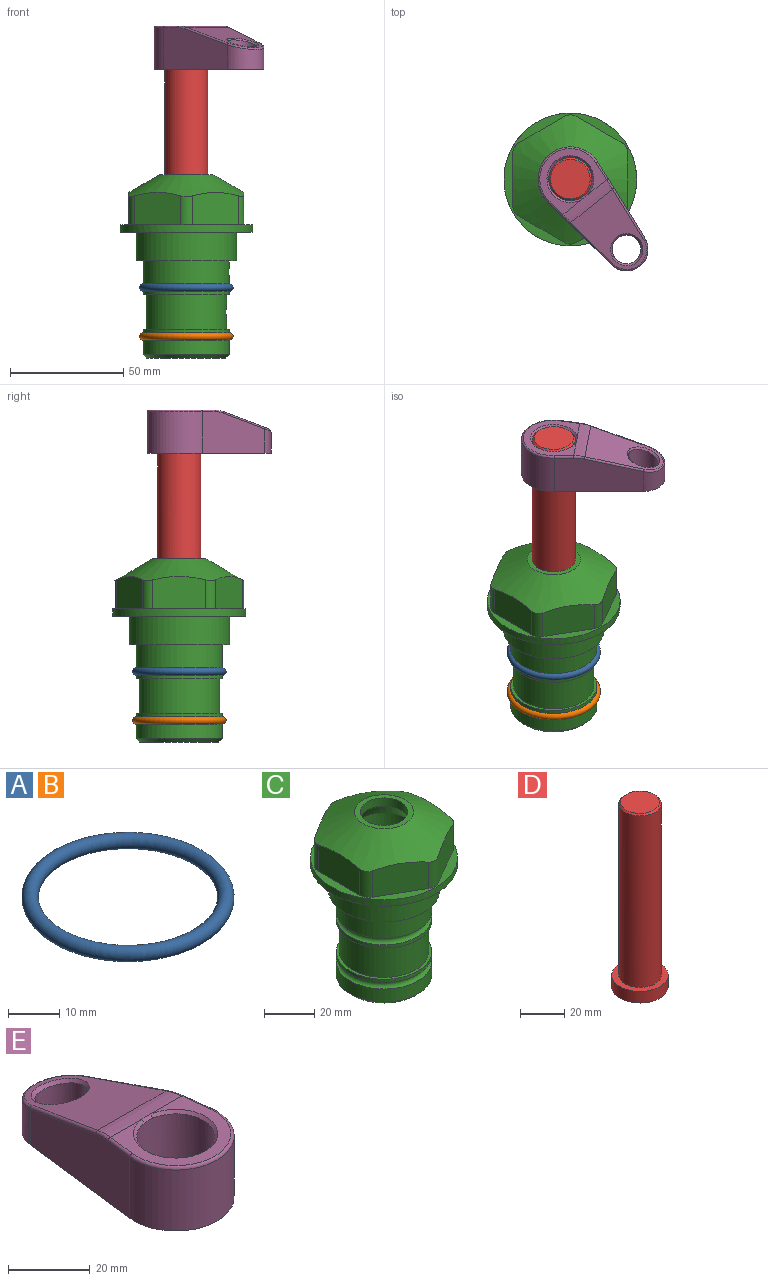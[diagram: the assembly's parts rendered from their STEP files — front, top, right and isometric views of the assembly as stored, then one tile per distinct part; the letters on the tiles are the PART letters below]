
ASSEMBLY  parts=5 mates=4
PART A: 1 faces, bbox 44.7x44.7x3.2 mm
  f0: torus R=19.05mm, axis (0,0,1), area 1193.9mm2
PART B: same geometry as A
PART C: 36 faces, bbox 58.7x58.7x81 mm
  f0: cylinder r=17.78mm len=35.56mm, axis (0,0,1), area 1670.8mm2, adj f23,f24,f31
  f1: cylinder r=19.05mm len=38.1mm, axis (0,0,1), area 1191.9mm2, adj f26,f27,f30
  f2: plane 58.66x58.66mm, normal (0,0,-1), area 1150.6mm2, adj f3,f28
  f3: cylinder r=29.33mm len=58.66mm, axis (0,0,-1), area 585.1mm2, adj f2,f4
  f4: plane 58.66x58.66mm, normal (0,0,1), area 475.9mm2, adj f3,f5,f6,f7,f8,f9,f10,f11
  f5: plane 20.32x14.34mm, normal (-0.5,0.87,0), area 324.4mm2, adj f4,f15,f16,f17
  f6: plane 20.32x14.34mm, normal (0.5,0.87,0), area 324.4mm2, adj f4,f14,f15,f17
  f7: plane 23.48x14.34mm, normal (1,0,0), area 324.4mm2, adj f4,f13,f14,f17
  f8: plane 20.32x14.34mm, normal (0.5,-0.87,0), area 324.4mm2, adj f4,f12,f13,f17
  f9: plane 20.32x14.34mm, normal (-0.5,-0.87,0), area 324.4mm2, adj f4,f11,f12,f17
  f10: plane 23.48x14.34mm, normal (-1,0,0), area 324.4mm2, adj f4,f11,f16,f17
  f11: cylinder r=5.08mm len=12.85mm, axis (0,0,-1), area 67.2mm2, adj f4,f9,f10,f17
  f12: cylinder r=5.08mm len=12.85mm, axis (0,0,-1), area 67.2mm2, adj f4,f8,f9,f17
  f13: cylinder r=5.08mm len=12.85mm, axis (0,0,-1), area 67.2mm2, adj f4,f7,f8,f17
  f14: cylinder r=5.08mm len=12.85mm, axis (0,0,-1), area 67.2mm2, adj f4,f6,f7,f17
  f15: cylinder r=5.08mm len=12.85mm, axis (0,0,-1), area 67.2mm2, adj f4,f5,f6,f17
  f16: cylinder r=5.08mm len=12.85mm, axis (0,0,-1), area 67.2mm2, adj f4,f5,f10,f17
  f17: cone r=11.73mm half-angle=60deg, axis (0,0,-1), area 2071.8mm2, adj f5,f6,f7,f8,f9,f10,f11,f12
  f18: plane 23.46x23.46mm, normal (0,0,1), area 147.4mm2, adj f17,f35
  f19: plane 34.93x34.93mm, normal (0,0,-1), area 958mm2, adj f29
  f20: cylinder r=19.05mm len=38.1mm, axis (0,0,1), area 760.1mm2, adj f21,f29
  f21: torus R=19.05mm, axis (0,0,1), area 565.3mm2, adj f20,f22
  f22: cylinder r=19.05mm len=38.1mm, axis (0,0,1), area 190mm2, adj f21,f23
  f23: plane 38.1x38.1mm, normal (0,0,1), area 146.9mm2, adj f0,f22
  f24: plane 38.1x38.1mm, normal (0,0,-1), area 146.9mm2, adj f0,f25
  f25: cylinder r=19.05mm len=38.1mm, axis (0,0,1), area 190mm2, adj f24,f26
  f26: torus R=19.05mm, axis (0,0,1), area 565.3mm2, adj f1,f25
  f27: plane 44.45x44.45mm, normal (0,0,-1), area 411.7mm2, adj f1,f28
  f28: cylinder r=22.23mm len=44.45mm, axis (0,0,1), area 1773.5mm2, adj f2,f27
  f29: cone r=19.05mm half-angle=45deg, axis (0,0,1), area 257.5mm2, adj f19,f20
  f30: cylinder r=3.17mm len=6.75mm, axis (-1,0,0), area 128mm2, adj f1,f33
  f31: cylinder r=3.17mm len=6.35mm, axis (-1,0,0), area 102.5mm2, adj f0,f33
  f32: plane 25.4x25.4mm, normal (0,0,1), area 506.7mm2, adj f33
  f33: cylinder r=12.7mm len=66.42mm, axis (0,0,-1), area 5236.2mm2, adj f30,f31,f32,f34
  f34: cone r=9.53mm half-angle=30deg, axis (0,0,-1), area 443.4mm2, adj f33,f35
  f35: cylinder r=9.53mm len=19.05mm, axis (0,0,-1), area 240.9mm2, adj f18,f34
PART D: 6 faces, bbox 25.4x25.4x101.6 mm
  f0: plane 17.46x17.46mm, normal (0,0,1), area 239.5mm2, adj f5
  f1: plane 25.4x25.4mm, normal (0,0,-1), area 506.7mm2, adj f2
  f2: cylinder r=12.7mm len=25.4mm, axis (0,0,1), area 506.7mm2, adj f1,f3
  f3: plane 25.4x25.4mm, normal (0,0,1), area 221.7mm2, adj f2,f4
  f4: cylinder r=9.53mm len=94.46mm, axis (0,0,1), area 5653mm2, adj f3,f5
  f5: cone r=8.73mm half-angle=45deg, axis (0,0,-1), area 64.4mm2, adj f0,f4
PART E: 31 faces, bbox 31.7x65.5x19.8 mm
  f0: plane 39.12x18.26mm, normal (0.99,0.12,0), area 612.2mm2, adj f1,f4,f7,f11,f13,f15
  f1: cylinder r=9.53mm len=18.91mm, axis (0,0,-1), area 296.1mm2, adj f0,f2,f7,f17
  f2: plane 39.12x18.26mm, normal (-0.99,0.12,0), area 612.2mm2, adj f1,f4,f7,f12,f14,f16
  f3: cylinder r=6.35mm len=12.7mm, axis (0,0,-1), area 362.4mm2, adj f7,f18
  f4: cylinder r=14.29mm len=28.58mm, axis (0,0,-1), area 882.2mm2, adj f0,f2,f7,f10
  f5: cylinder r=9.53mm len=19.05mm, axis (0,0,-1), area 1092.6mm2, adj f7,f19,f20
  f6: plane 26.99x23.69mm, normal (0,0,1), area 216.2mm2, adj f9,f10,f11,f12,f19
  f7: plane 63.5x28.58mm, normal (0,0,-1), area 661.8mm2, adj f0,f1,f2,f3,f4,f5,f22,f23
  f8: plane 33.52x23.6mm, normal (0,0.26,0.97), area 486mm2, adj f9,f15,f16,f17,f18
  f9: cylinder r=19.05mm len=24.72mm, axis (1,0,0), area 120.4mm2, adj f6,f8,f13,f14,f20
  f10: torus R=13.49mm, axis (0,0,1), area 59mm2, adj f4,f6,f11,f12
  f11: cylinder r=0.79mm len=8.67mm, axis (0.12,-0.99,0), area 10.8mm2, adj f0,f6,f10,f13
  f12: cylinder r=0.79mm len=8.67mm, axis (0.12,0.99,0), area 10.8mm2, adj f2,f6,f10,f14
  f13: bspline ~4.95x1.42mm, area 6.1mm2, adj f0,f9,f11,f15
  f14: bspline ~4.95x1.42mm, area 6.1mm2, adj f2,f9,f12,f16
  f15: cylinder r=0.79mm len=25.95mm, axis (0.12,-0.96,0.26), area 32.9mm2, adj f0,f8,f13,f17
  f16: cylinder r=0.79mm len=25.95mm, axis (0.12,0.96,-0.26), area 32.9mm2, adj f2,f8,f14,f17
  f17: bspline ~18.91x8.38mm, area 30mm2, adj f1,f8,f15,f16
  f18: bspline ~14.29x14.29mm, area 48.3mm2, adj f3,f8
  f19: cone r=9.53mm half-angle=45deg, axis (0,0,1), area 66.5mm2, adj f5,f6,f20
  f20: bspline ~3.22x0.96mm, area 3.5mm2, adj f5,f9,f19
  f21: plane 2.75x2.72mm, normal (0,0,-1), area 2.9mm2, adj f23,f25,f28
  f22: plane 23.05x15.88mm, normal (-0.99,-0.12,0), area 323.6mm2, adj f7,f25,f26,f27,f28,f29
  f23: plane 23.05x15.88mm, normal (0.99,-0.12,0), area 323.6mm2, adj f7,f21,f25,f27,f28,f30
  f24: cylinder r=9.53mm len=10.69mm, axis (0,0,-1), area 114.7mm2, adj f7,f27,f29,f30
  f25: cylinder r=12.7mm len=20.59mm, axis (0,0,-1), area 381.1mm2, adj f7,f21,f22,f23,f26,f28
  f26: plane 2.75x2.72mm, normal (0,0,-1), area 2.9mm2, adj f22,f25,f28
  f27: plane 19.72x18.37mm, normal (0,-0.26,-0.97), area 291.8mm2, adj f22,f23,f24,f28,f29,f30
  f28: cylinder r=15.88mm len=19.92mm, axis (1,0,0), area 54.8mm2, adj f21,f22,f23,f25,f26,f27
  f29: cylinder r=1.59mm len=11mm, axis (0,0,-1), area 34.7mm2, adj f7,f22,f24,f27
  f30: cylinder r=1.59mm len=11mm, axis (0,0,-1), area 34.7mm2, adj f7,f23,f24,f27
PLACE A at identity
PLACE B t=(0,0,-21.59)mm
PLACE C at identity fixed
PLACE D rot(axis=(0,0,-1),141.4deg) t=(0,0,27.55)mm
PLACE E rot(axis=(0,0,-1),141.4deg) t=(0,0,27.55)mm
MATE fastened C.f0 <-> A.f0  axis (0,0,1) through (0,0,-24.51)mm
MATE cylindrical D.f2 <-> C.f0  axis (0,0,-1) through (0,0,-10.55)mm
MATE fastened C.f0 <-> B.f0  axis (0,0,1) through (0,0,-46.1)mm
MATE fastened D.f2 <-> E.f4  axis (0,0,1) through (0,0,91.05)mm
